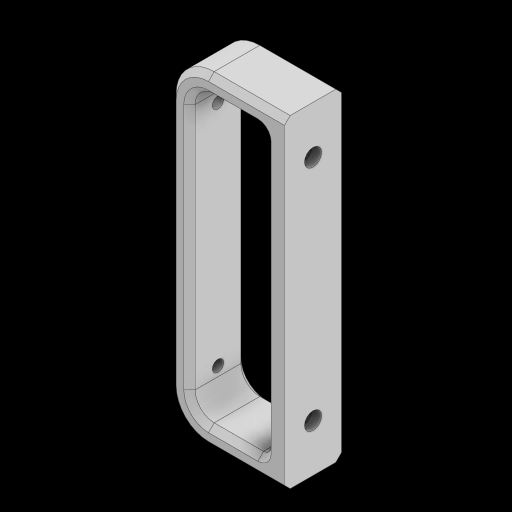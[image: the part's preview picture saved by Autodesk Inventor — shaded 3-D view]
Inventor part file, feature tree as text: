
AUTODESK INVENTOR PART (.ipt)
format: ipt  version: 2024 (Build 280153000, 153)  size: 194,560 bytes
history: native  units: mm
features: fillet x3, sketch x3, hole x2, chamfer x2, extrude x1
ambient origin geometry x8: Origin, YZ Plane, XZ Plane, XY Plane, X Axis, Y Axis, Z Axis, Center Point
bodies: Volumenkörper1 (feature_tree)
feature tree (11):
  extrude  "Extrusion1"  Depth=85.0mm
  fillet  "Rundung1"  Radius=25.0mm
  fillet  "Rundung2"  Radius=5.0mm
  fillet  "Rundung3"  Radius=5.0mm
  hole  "Bohrung1"  [1 undecoded]
  hole  "Bohrung2"  [1 undecoded]
  chamfer  "Fasen1"  Distance=2.0mm
  chamfer  "Fasen2"  Distance=30.0mm
  sketch  "Skizze1"  dims[d0=5.0mm d1=85.0mm d2=25.0mm d3=5.0mm d4=5.0mm]
  sketch  "Skizze2"  dims[d5=85.0mm d6=15.0mm d7=0.0mm]
  sketch  "Skizze3"  dims[d8=10.0mm d9=5.0mm d10=2.0mm d13=30.0mm d14=5.0mm d15=60.0mm d16=12.5mm d17=4.5mm d18=6.0mm d19=9.4mm d20=2.0mm d21=90.0deg d22=8.0mm d23=20.594885mm d24=3.0mm d25=6.0mm d26=9.4mm d27=2.0mm d28=90.0deg d29=8.0mm d30=20.594885mm d31=1.5mm d32=2.0mm d33=45.0deg d34=1.5mm d35=2.0mm d36=45.0deg]
note: 2 required parameter values undecoded (feature->parameter linkage not recoverable at this tier; creation-order binding heuristic only, values carry confidence <= 0.55)
